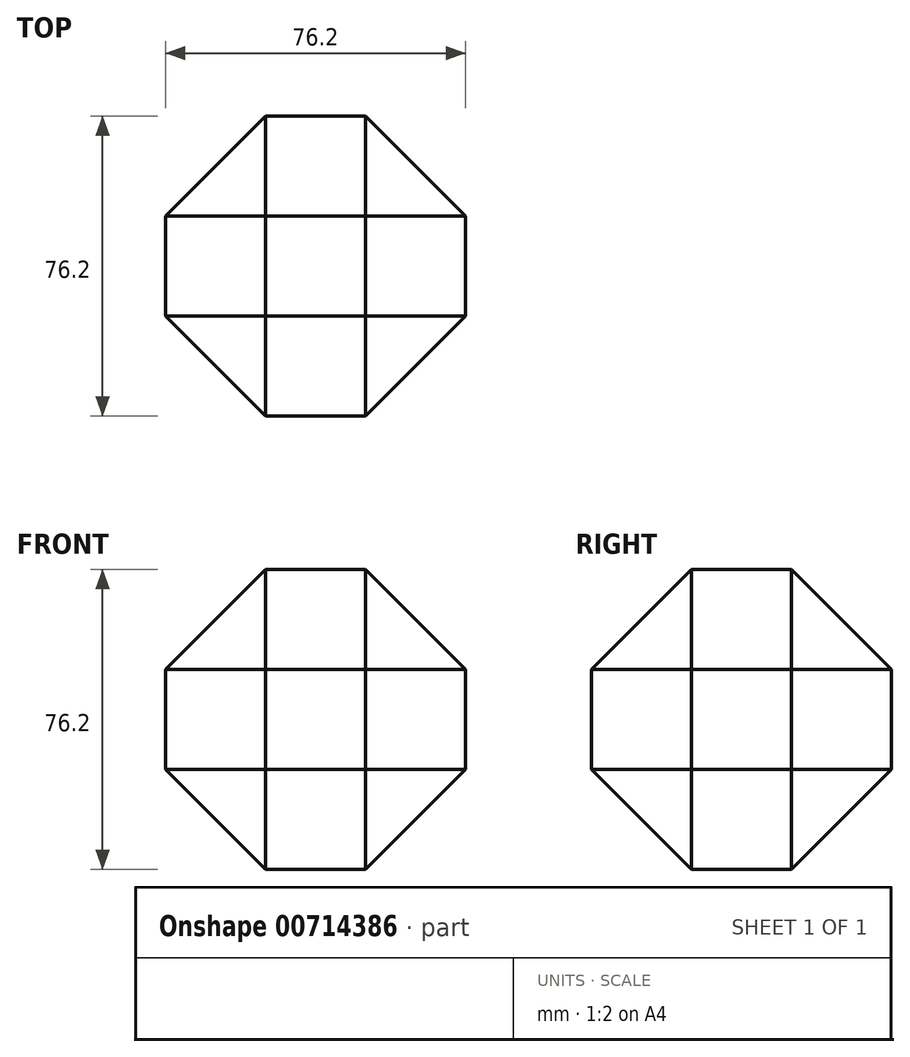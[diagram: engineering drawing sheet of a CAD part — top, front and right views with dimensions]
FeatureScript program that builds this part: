
annotation { "Feature Type Name" : "Feature", "Feature Type Description" : "" }
export const myFeature = defineFeature(function(context is Context, id is Id, definition is map)
    precondition{}
    {
        {
            var Q0;
            Q0=qCreatedBy(makeId("Top.planeOp"),FACE);
            var sketch = newSketch(context, id + "F0", { "sketchPlane" : qUnion([Q0])});
            skLineSegment(sketch, "E0.bottom", {"start": v(-38.1, -38.1) * mm, "end": v(38.1, -38.1) * mm});
            skLineSegment(sketch, "E0.top", {"start": v(-38.1, 38.1) * mm, "end": v(38.1, 38.1) * mm});
            skLineSegment(sketch, "E0.left", {"start": v(-38.1, -38.1) * mm, "end": v(-38.1, 38.1) * mm});
            skLineSegment(sketch, "E0.right", {"start": v(38.1, -38.1) * mm, "end": v(38.1, 38.1) * mm});
            skPoint(sketch, "E0.middle", {"position": v(0, 0) * mm});
            skSolve(sketch);
        }
        {
            var Q0;
            Q0=makeQuery(id+"F0.imprint","IMPRINT",FACE,{"disambiguationData":[TD([[makeQuery(id+"F0.imprint","IMPRINT",EDGE,{"derivedFrom":sQuery(id+"F0.wireOp",EDGE,"E0.bottom")}),1.0]])]});
            extrude(context, id + "F1", {"entities" : qUnion([Q0]), "depth" : 76.2 * mm, "offsetDistance" : 25.4 * mm});
        }
        {
            var Q0;
            Q0=makeQuery(id+"F1.opExtrude","SWEPT_FACE",FACE,{"disambiguationData":[OSD([sQuery(id+"F0.wireOp",EDGE,"E0.bottom")])]});
            var Q1;
            Q1=makeQuery(id+"F1.opExtrude","CAP_FACE",FACE,{"disambiguationData":[OSD([sQuery(id+"F0.wireOp",EDGE,"E0.bottom"),sQuery(id+"F0.wireOp",EDGE,"E0.top"),sQuery(id+"F0.wireOp",EDGE,"E0.left"),sQuery(id+"F0.wireOp",EDGE,"E0.right")])],"isStart":true});
            var Q2;
            Q2=makeQuery(id+"F1.opExtrude","SWEPT_FACE",FACE,{"disambiguationData":[OSD([sQuery(id+"F0.wireOp",EDGE,"E0.top")])]});
            var Q3;
            Q3=makeQuery(id+"F1.opExtrude","CAP_FACE",FACE,{"disambiguationData":[OSD([sQuery(id+"F0.wireOp",EDGE,"E0.bottom"),sQuery(id+"F0.wireOp",EDGE,"E0.top"),sQuery(id+"F0.wireOp",EDGE,"E0.left"),sQuery(id+"F0.wireOp",EDGE,"E0.right")])],"isStart":false});
            var Q4;
            Q4=makeQuery(id+"F1.opExtrude","SWEPT_FACE",FACE,{"disambiguationData":[OSD([sQuery(id+"F0.wireOp",EDGE,"E0.left")])]});
            chamfer(context, id + "F2", {"entities" : qUnion([Q0, Q1, Q2, Q3, Q4]), "width" : 25.4 * mm, "tangentPropagation" : true});
        }
    });
